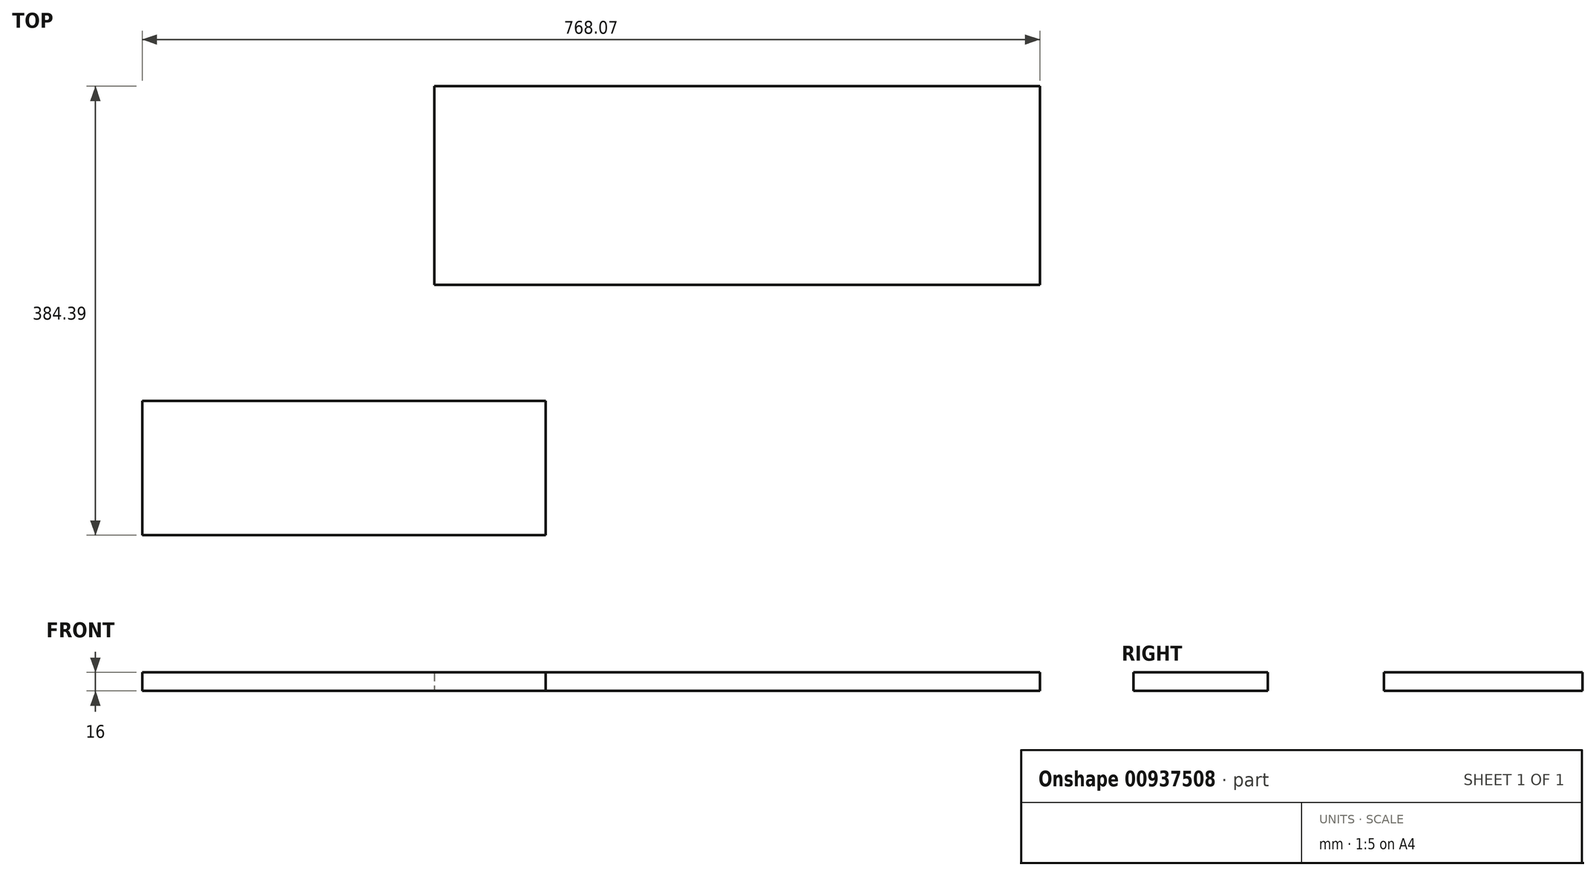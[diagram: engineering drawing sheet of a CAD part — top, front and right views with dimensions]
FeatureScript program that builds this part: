
annotation { "Feature Type Name" : "Feature", "Feature Type Description" : "" }
export const myFeature = defineFeature(function(context is Context, id is Id, definition is map)
    precondition{}
    {
        {
            var Q0;
            Q0=qCreatedBy(makeId("Top.planeOp"),FACE);
            var sketch = newSketch(context, id + "F0", { "sketchPlane" : qUnion([Q0])});
            skLineSegment(sketch, "E0.bottom", {"start": v(-384.28, 483.73) * mm, "end": v(133.72, 483.73) * mm});
            skLineSegment(sketch, "E0.top", {"start": v(-384.28, 313.73) * mm, "end": v(133.72, 313.73) * mm});
            skLineSegment(sketch, "E0.left", {"start": v(-384.28, 483.73) * mm, "end": v(-384.28, 313.73) * mm});
            skLineSegment(sketch, "E0.right", {"start": v(133.72, 483.73) * mm, "end": v(133.72, 313.73) * mm});
            skLineSegment(sketch, "E1.bottom", {"start": v(-289.17, 99.34) * mm, "end": v(-634.35, 99.34) * mm});
            skLineSegment(sketch, "E1.top", {"start": v(-289.17, 214.4) * mm, "end": v(-634.35, 214.4) * mm});
            skLineSegment(sketch, "E1.left", {"start": v(-289.17, 99.34) * mm, "end": v(-289.17, 214.4) * mm});
            skLineSegment(sketch, "E1.right", {"start": v(-634.35, 99.34) * mm, "end": v(-634.35, 214.4) * mm});
            skPoint(sketch, "E1.middle", {"position": v(-461.76, 156.87) * mm});
            skSolve(sketch);
        }
        {
            assignVariable(context, id + "F1", {"name" : "espesor", "anyValue" : 16});
        }
        {
            var Q0;
            Q0=makeQuery(id+"F0.imprint","IMPRINT",FACE,{"disambiguationData":[TD([[makeQuery(id+"F0.imprint","IMPRINT",EDGE,{"derivedFrom":sQuery(id+"F0.wireOp",EDGE,"E0.bottom")}),-1.0]])]});
            var Q1;
            Q1=makeQuery(id+"F0.imprint","IMPRINT",FACE,{"disambiguationData":[TD([[makeQuery(id+"F0.imprint","IMPRINT",EDGE,{"derivedFrom":sQuery(id+"F0.wireOp",EDGE,"E1.bottom")}),-1.0]])]});
            extrude(context, id + "F2", {"entities" : qUnion([Q0, Q1]), "depth" : getVariable(context, 'espesor') * mm, "offsetDistance" : 25 * mm});
        }
    });
